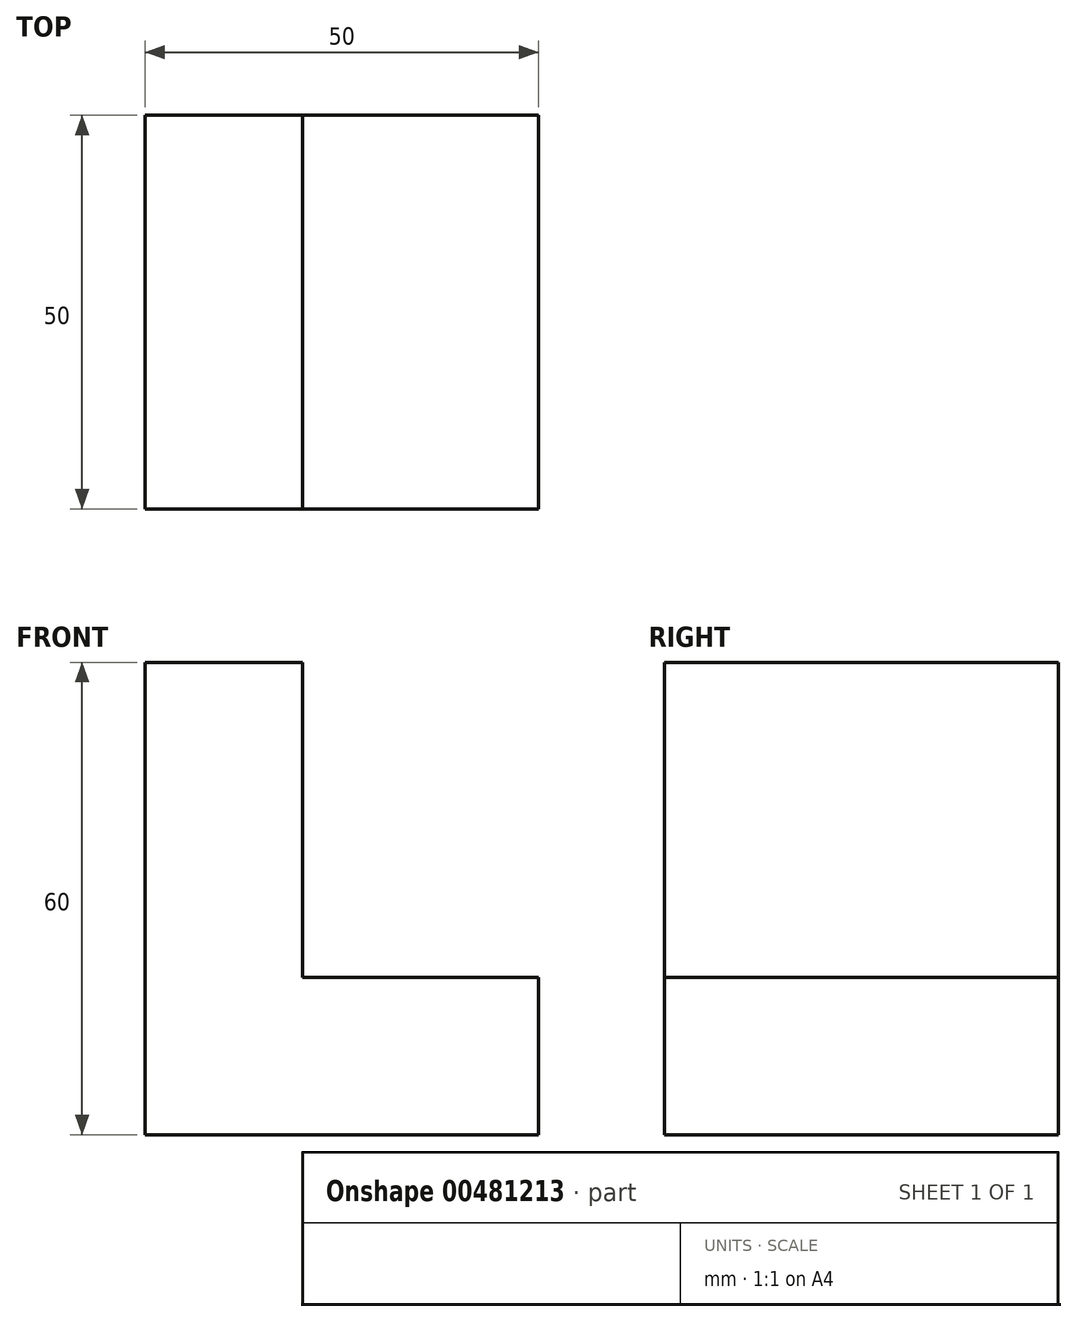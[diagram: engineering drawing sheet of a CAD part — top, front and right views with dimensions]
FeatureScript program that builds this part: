
annotation { "Feature Type Name" : "Feature", "Feature Type Description" : "" }
export const myFeature = defineFeature(function(context is Context, id is Id, definition is map)
    precondition{}
    {
        {
            var Q0;
            Q0=qCreatedBy(makeId("Front.planeOp"),FACE);
            var sketch = newSketch(context, id + "F0", { "sketchPlane" : qUnion([Q0])});
            skLineSegment(sketch, "E0", {"start": v(0, 0) * mm, "end": v(0, 60) * mm});
            skLineSegment(sketch, "E1", {"start": v(0, 60) * mm, "end": v(20, 60) * mm});
            skLineSegment(sketch, "E2", {"start": v(20, 60) * mm, "end": v(20, 20) * mm});
            skLineSegment(sketch, "E3", {"start": v(20, 20) * mm, "end": v(50, 20) * mm});
            skLineSegment(sketch, "E4", {"start": v(50, 20) * mm, "end": v(50, 0) * mm});
            skLineSegment(sketch, "E5", {"start": v(50, 0) * mm, "end": v(0, 0) * mm});
            skSolve(sketch);
        }
        {
            var Q0;
            Q0=makeQuery(id+"F0.imprint","IMPRINT",FACE,{"disambiguationData":[TD([[makeQuery(id+"F0.imprint","IMPRINT",EDGE,{"derivedFrom":sQuery(id+"F0.wireOp",EDGE,"E0")}),-1.0]])]});
            extrude(context, id + "F1", {"entities" : qUnion([Q0]), "depth" : 50 * mm});
        }
    });
